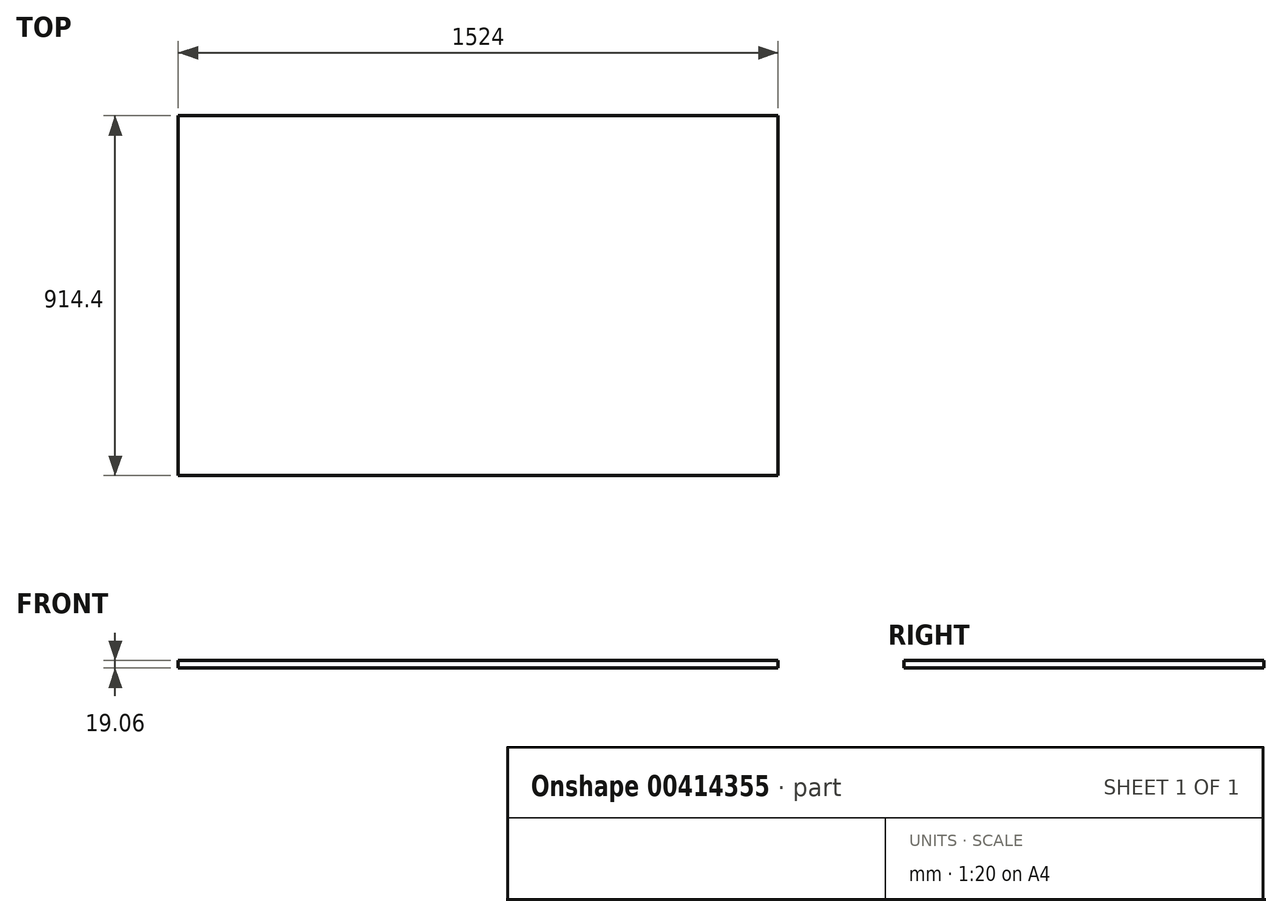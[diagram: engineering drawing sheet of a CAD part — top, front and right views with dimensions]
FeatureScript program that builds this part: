
annotation { "Feature Type Name" : "Feature", "Feature Type Description" : "" }
export const myFeature = defineFeature(function(context is Context, id is Id, definition is map)
    precondition{}
    {
        {
            var Q0;
            Q0=qCreatedBy(makeId("Top.planeOp"),FACE);
            var sketch = newSketch(context, id + "F0", { "sketchPlane" : qUnion([Q0])});
            skLineSegment(sketch, "E0.bottom", {"start": v(762, -457.2) * mm, "end": v(-762, -457.2) * mm});
            skLineSegment(sketch, "E0.top", {"start": v(762, 457.2) * mm, "end": v(-762, 457.2) * mm});
            skLineSegment(sketch, "E0.left", {"start": v(762, -457.2) * mm, "end": v(762, 457.2) * mm});
            skLineSegment(sketch, "E0.right", {"start": v(-762, -457.2) * mm, "end": v(-762, 457.2) * mm});
            skPoint(sketch, "E0.middle", {"position": v(0, 0) * mm});
            skSolve(sketch);
        }
        {
            var Q0;
            Q0 = qSketchRegion(id + "F0", true);
            extrude(context, id + "F1", {"entities" : qUnion([Q0]), "endBound" : BoundingType.SYMMETRIC, "depth" : 19.05 * mm});
        }
    });
